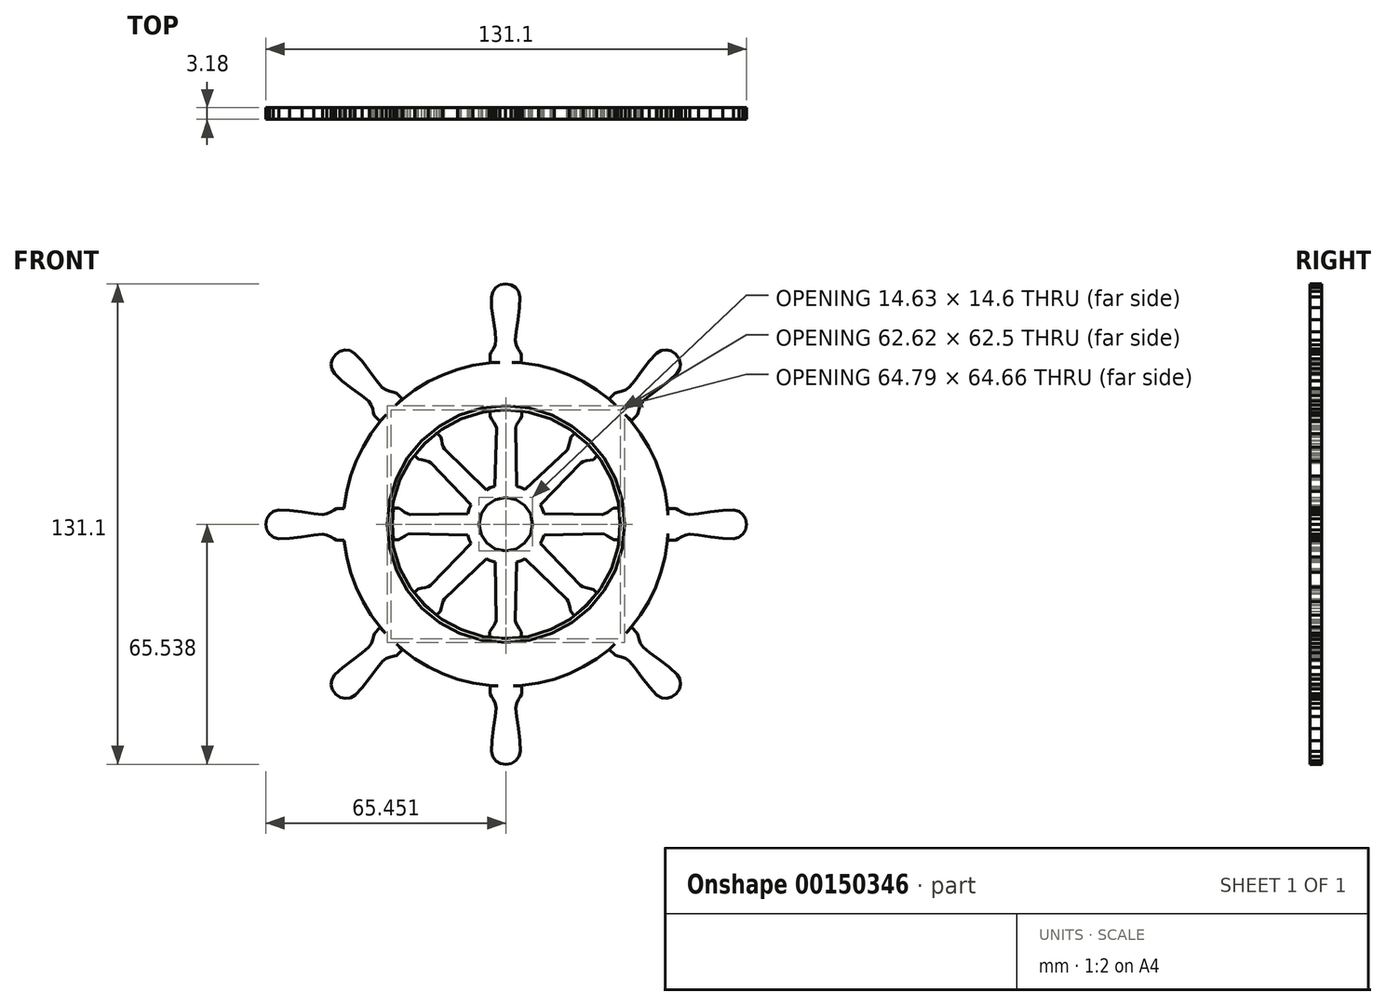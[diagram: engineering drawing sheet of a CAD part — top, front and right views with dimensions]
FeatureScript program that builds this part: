
annotation { "Feature Type Name" : "Feature", "Feature Type Description" : "" }
export const myFeature = defineFeature(function(context is Context, id is Id, definition is map)
    precondition{}
    {
        {
            var Q0;
            Q0=qCreatedBy(makeId("Front.planeOp"),FACE);
            var sketch = newSketch(context, id + "F0", { "sketchPlane" : qUnion([Q0])});
            skLineSegment(sketch, "E0", {"start": v(-9.65, -2.99) * mm, "end": v(-26.1, -2.56) * mm});
            skLineSegment(sketch, "E1", {"start": v(-26.1, -2.56) * mm, "end": v(-26.82, -2.77) * mm});
            skLineSegment(sketch, "E2", {"start": v(-26.82, -2.77) * mm, "end": v(-27.64, -3.22) * mm});
            skLineSegment(sketch, "E3", {"start": v(-27.64, -3.22) * mm, "end": v(-28.5, -3.78) * mm});
            skLineSegment(sketch, "E4", {"start": v(-28.5, -3.78) * mm, "end": v(-29.36, -4.29) * mm});
            skLineSegment(sketch, "E5", {"start": v(-29.36, -4.29) * mm, "end": v(-30.78, -4.29) * mm});
            skLineSegment(sketch, "E6", {"start": v(-30.78, -4.29) * mm, "end": v(-31.08, 0.04) * mm});
            skLineSegment(sketch, "E7", {"start": v(-31.08, 0.04) * mm, "end": v(-30.78, 4.37) * mm});
            skLineSegment(sketch, "E8", {"start": v(-30.78, 4.37) * mm, "end": v(-29.29, 4.37) * mm});
            skLineSegment(sketch, "E9", {"start": v(-29.29, 4.37) * mm, "end": v(-28.5, 3.85) * mm});
            skLineSegment(sketch, "E10", {"start": v(-28.5, 3.85) * mm, "end": v(-27.69, 3.29) * mm});
            skLineSegment(sketch, "E11", {"start": v(-27.69, 3.29) * mm, "end": v(-26.91, 2.84) * mm});
            skLineSegment(sketch, "E12", {"start": v(-26.91, 2.84) * mm, "end": v(-26.22, 2.67) * mm});
            skLineSegment(sketch, "E13", {"start": v(-26.22, 2.67) * mm, "end": v(-9.66, 2.93) * mm});
            skLineSegment(sketch, "E14", {"start": v(-29.33, -4.38) * mm, "end": v(-29.55, 0) * mm});
            skLineSegment(sketch, "E15", {"start": v(-29.55, 0) * mm, "end": v(-29.33, 4.44) * mm});
            skLineSegment(sketch, "E16", {"start": v(-62.02, -3.96) * mm, "end": v(-59.16, -3.9) * mm});
            skLineSegment(sketch, "E17", {"start": v(-59.16, -3.9) * mm, "end": v(-55.76, -3.45) * mm});
            skLineSegment(sketch, "E18", {"start": v(-55.76, -3.45) * mm, "end": v(-52.53, -2.95) * mm});
            skLineSegment(sketch, "E19", {"start": v(-52.53, -2.95) * mm, "end": v(-50.15, -2.7) * mm});
            skLineSegment(sketch, "E20", {"start": v(-50.15, -2.7) * mm, "end": v(-48.91, -2.92) * mm});
            skLineSegment(sketch, "E21", {"start": v(-48.91, -2.92) * mm, "end": v(-47.83, -3.44) * mm});
            skLineSegment(sketch, "E22", {"start": v(-47.83, -3.44) * mm, "end": v(-46.94, -3.98) * mm});
            skLineSegment(sketch, "E23", {"start": v(-46.94, -3.98) * mm, "end": v(-46.3, -4.31) * mm});
            skLineSegment(sketch, "E24", {"start": v(-46.3, -4.31) * mm, "end": v(-44.13, -4.33) * mm});
            skLineSegment(sketch, "E25", {"start": v(-44.13, -4.33) * mm, "end": v(-44.13, 4.25) * mm});
            skLineSegment(sketch, "E26", {"start": v(-44.13, 4.25) * mm, "end": v(-46.3, 4.23) * mm});
            skLineSegment(sketch, "E27", {"start": v(-46.3, 4.23) * mm, "end": v(-46.94, 3.9) * mm});
            skLineSegment(sketch, "E28", {"start": v(-46.94, 3.9) * mm, "end": v(-47.83, 3.36) * mm});
            skLineSegment(sketch, "E29", {"start": v(-47.83, 3.36) * mm, "end": v(-48.91, 2.85) * mm});
            skLineSegment(sketch, "E30", {"start": v(-48.91, 2.85) * mm, "end": v(-50.15, 2.62) * mm});
            skLineSegment(sketch, "E31", {"start": v(-50.15, 2.62) * mm, "end": v(-52.53, 2.85) * mm});
            skLineSegment(sketch, "E32", {"start": v(-52.53, 2.85) * mm, "end": v(-55.75, 3.32) * mm});
            skLineSegment(sketch, "E33", {"start": v(-55.75, 3.32) * mm, "end": v(-59.15, 3.75) * mm});
            skLineSegment(sketch, "E34", {"start": v(-59.15, 3.75) * mm, "end": v(-62.02, 3.87) * mm});
            skLineSegment(sketch, "E35", {"start": v(-62.02, 3.87) * mm, "end": v(-63.52, 3.5) * mm});
            skLineSegment(sketch, "E36", {"start": v(-63.52, 3.5) * mm, "end": v(-64.63, 2.66) * mm});
            skLineSegment(sketch, "E37", {"start": v(-64.63, 2.66) * mm, "end": v(-65.32, 1.44) * mm});
            skLineSegment(sketch, "E38", {"start": v(-65.32, 1.44) * mm, "end": v(-65.55, -0.04) * mm});
            skLineSegment(sketch, "E39", {"start": v(-65.55, -0.04) * mm, "end": v(-65.3, -1.56) * mm});
            skLineSegment(sketch, "E40", {"start": v(-65.3, -1.56) * mm, "end": v(-64.57, -2.76) * mm});
            skLineSegment(sketch, "E41", {"start": v(-64.57, -2.76) * mm, "end": v(-63.45, -3.57) * mm});
            skLineSegment(sketch, "E42", {"start": v(-63.45, -3.57) * mm, "end": v(-62.02, -3.96) * mm});
            skLineSegment(sketch, "E43", {"start": v(-46.16, -4.38) * mm, "end": v(-46.53, -0.02) * mm});
            skLineSegment(sketch, "E44", {"start": v(-46.53, -0.02) * mm, "end": v(-46.16, 4.33) * mm});
            skLineSegment(sketch, "E45", {"start": v(2.89, -9.76) * mm, "end": v(2.46, -26.18) * mm});
            skLineSegment(sketch, "E46", {"start": v(2.46, -26.18) * mm, "end": v(2.67, -26.9) * mm});
            skLineSegment(sketch, "E47", {"start": v(2.67, -26.9) * mm, "end": v(3.12, -27.72) * mm});
            skLineSegment(sketch, "E48", {"start": v(3.12, -27.72) * mm, "end": v(3.68, -28.58) * mm});
            skLineSegment(sketch, "E49", {"start": v(3.68, -28.58) * mm, "end": v(4.19, -29.44) * mm});
            skLineSegment(sketch, "E50", {"start": v(4.19, -29.44) * mm, "end": v(4.19, -30.85) * mm});
            skLineSegment(sketch, "E51", {"start": v(4.19, -30.85) * mm, "end": v(-0.15, -31.15) * mm});
            skLineSegment(sketch, "E52", {"start": v(-0.15, -31.15) * mm, "end": v(-4.49, -30.85) * mm});
            skLineSegment(sketch, "E53", {"start": v(-4.49, -30.85) * mm, "end": v(-4.49, -29.36) * mm});
            skLineSegment(sketch, "E54", {"start": v(-4.49, -29.36) * mm, "end": v(-3.97, -28.57) * mm});
            skLineSegment(sketch, "E55", {"start": v(-3.97, -28.57) * mm, "end": v(-3.4, -27.76) * mm});
            skLineSegment(sketch, "E56", {"start": v(-3.4, -27.76) * mm, "end": v(-2.96, -27) * mm});
            skLineSegment(sketch, "E57", {"start": v(-2.96, -27) * mm, "end": v(-2.79, -26.3) * mm});
            skLineSegment(sketch, "E58", {"start": v(-2.79, -26.3) * mm, "end": v(-3.05, -9.77) * mm});
            skLineSegment(sketch, "E59", {"start": v(4.28, -29.4) * mm, "end": v(-0.1, -29.62) * mm});
            skLineSegment(sketch, "E60", {"start": v(-0.1, -29.62) * mm, "end": v(-4.56, -29.4) * mm});
            skLineSegment(sketch, "E61", {"start": v(3.86, -62.02) * mm, "end": v(3.79, -59.17) * mm});
            skLineSegment(sketch, "E62", {"start": v(3.79, -59.17) * mm, "end": v(3.34, -55.78) * mm});
            skLineSegment(sketch, "E63", {"start": v(3.34, -55.78) * mm, "end": v(2.84, -52.55) * mm});
            skLineSegment(sketch, "E64", {"start": v(2.84, -52.55) * mm, "end": v(2.6, -50.18) * mm});
            skLineSegment(sketch, "E65", {"start": v(2.6, -50.18) * mm, "end": v(2.82, -48.95) * mm});
            skLineSegment(sketch, "E66", {"start": v(2.82, -48.95) * mm, "end": v(3.33, -47.86) * mm});
            skLineSegment(sketch, "E67", {"start": v(3.33, -47.86) * mm, "end": v(3.88, -46.98) * mm});
            skLineSegment(sketch, "E68", {"start": v(3.88, -46.98) * mm, "end": v(4.21, -46.34) * mm});
            skLineSegment(sketch, "E69", {"start": v(4.21, -46.34) * mm, "end": v(4.23, -44.17) * mm});
            skLineSegment(sketch, "E70", {"start": v(4.23, -44.17) * mm, "end": v(-4.37, -44.17) * mm});
            skLineSegment(sketch, "E71", {"start": v(-4.37, -44.17) * mm, "end": v(-4.35, -46.34) * mm});
            skLineSegment(sketch, "E72", {"start": v(-4.35, -46.34) * mm, "end": v(-4.02, -46.98) * mm});
            skLineSegment(sketch, "E73", {"start": v(-4.02, -46.98) * mm, "end": v(-3.48, -47.86) * mm});
            skLineSegment(sketch, "E74", {"start": v(-3.48, -47.86) * mm, "end": v(-2.96, -48.95) * mm});
            skLineSegment(sketch, "E75", {"start": v(-2.96, -48.95) * mm, "end": v(-2.74, -50.18) * mm});
            skLineSegment(sketch, "E76", {"start": v(-2.74, -50.18) * mm, "end": v(-2.97, -52.55) * mm});
            skLineSegment(sketch, "E77", {"start": v(-2.97, -52.55) * mm, "end": v(-3.44, -55.77) * mm});
            skLineSegment(sketch, "E78", {"start": v(-3.44, -55.77) * mm, "end": v(-3.87, -59.16) * mm});
            skLineSegment(sketch, "E79", {"start": v(-3.87, -59.16) * mm, "end": v(-3.99, -62.02) * mm});
            skLineSegment(sketch, "E80", {"start": v(-3.99, -62.02) * mm, "end": v(-3.62, -63.52) * mm});
            skLineSegment(sketch, "E81", {"start": v(-3.62, -63.52) * mm, "end": v(-2.77, -64.63) * mm});
            skLineSegment(sketch, "E82", {"start": v(-2.77, -64.63) * mm, "end": v(-1.55, -65.31) * mm});
            skLineSegment(sketch, "E83", {"start": v(-1.55, -65.31) * mm, "end": v(-0.07, -65.55) * mm});
            skLineSegment(sketch, "E84", {"start": v(-0.07, -65.55) * mm, "end": v(1.46, -65.3) * mm});
            skLineSegment(sketch, "E85", {"start": v(1.46, -65.3) * mm, "end": v(2.65, -64.57) * mm});
            skLineSegment(sketch, "E86", {"start": v(2.65, -64.57) * mm, "end": v(3.47, -63.46) * mm});
            skLineSegment(sketch, "E87", {"start": v(3.47, -63.46) * mm, "end": v(3.86, -62.02) * mm});
            skLineSegment(sketch, "E88", {"start": v(4.27, -46.2) * mm, "end": v(-0.09, -46.56) * mm});
            skLineSegment(sketch, "E89", {"start": v(-0.09, -46.56) * mm, "end": v(-4.45, -46.2) * mm});
            skLineSegment(sketch, "E90", {"start": v(-3.08, 9.76) * mm, "end": v(-2.66, 26.18) * mm});
            skLineSegment(sketch, "E91", {"start": v(-2.66, 26.18) * mm, "end": v(-2.86, 26.9) * mm});
            skLineSegment(sketch, "E92", {"start": v(-2.86, 26.9) * mm, "end": v(-3.32, 27.72) * mm});
            skLineSegment(sketch, "E93", {"start": v(-3.32, 27.72) * mm, "end": v(-3.88, 28.58) * mm});
            skLineSegment(sketch, "E94", {"start": v(-3.88, 28.58) * mm, "end": v(-4.38, 29.44) * mm});
            skLineSegment(sketch, "E95", {"start": v(-4.38, 29.44) * mm, "end": v(-4.38, 30.85) * mm});
            skLineSegment(sketch, "E96", {"start": v(-4.38, 30.85) * mm, "end": v(-0.05, 31.15) * mm});
            skLineSegment(sketch, "E97", {"start": v(-0.05, 31.15) * mm, "end": v(4.29, 30.85) * mm});
            skLineSegment(sketch, "E98", {"start": v(4.29, 30.85) * mm, "end": v(4.29, 29.36) * mm});
            skLineSegment(sketch, "E99", {"start": v(4.29, 29.36) * mm, "end": v(3.77, 28.57) * mm});
            skLineSegment(sketch, "E100", {"start": v(3.77, 28.57) * mm, "end": v(3.2, 27.76) * mm});
            skLineSegment(sketch, "E101", {"start": v(3.2, 27.76) * mm, "end": v(2.76, 27) * mm});
            skLineSegment(sketch, "E102", {"start": v(2.76, 27) * mm, "end": v(2.59, 26.3) * mm});
            skLineSegment(sketch, "E103", {"start": v(2.59, 26.3) * mm, "end": v(2.85, 9.77) * mm});
            skLineSegment(sketch, "E104", {"start": v(-4.48, 29.4) * mm, "end": v(-0.1, 29.62) * mm});
            skLineSegment(sketch, "E105", {"start": v(-0.1, 29.62) * mm, "end": v(4.36, 29.4) * mm});
            skLineSegment(sketch, "E106", {"start": v(-4.05, 62.02) * mm, "end": v(-3.99, 59.17) * mm});
            skLineSegment(sketch, "E107", {"start": v(-3.99, 59.17) * mm, "end": v(-3.54, 55.78) * mm});
            skLineSegment(sketch, "E108", {"start": v(-3.54, 55.78) * mm, "end": v(-3.04, 52.56) * mm});
            skLineSegment(sketch, "E109", {"start": v(-3.04, 52.56) * mm, "end": v(-2.8, 50.18) * mm});
            skLineSegment(sketch, "E110", {"start": v(-2.8, 50.18) * mm, "end": v(-3.02, 48.95) * mm});
            skLineSegment(sketch, "E111", {"start": v(-3.02, 48.95) * mm, "end": v(-3.53, 47.86) * mm});
            skLineSegment(sketch, "E112", {"start": v(-3.53, 47.86) * mm, "end": v(-4.08, 46.98) * mm});
            skLineSegment(sketch, "E113", {"start": v(-4.08, 46.98) * mm, "end": v(-4.4, 46.34) * mm});
            skLineSegment(sketch, "E114", {"start": v(-4.4, 46.34) * mm, "end": v(-4.43, 44.17) * mm});
            skLineSegment(sketch, "E115", {"start": v(-4.43, 44.17) * mm, "end": v(4.17, 44.17) * mm});
            skLineSegment(sketch, "E116", {"start": v(4.17, 44.17) * mm, "end": v(4.15, 46.34) * mm});
            skLineSegment(sketch, "E117", {"start": v(4.15, 46.34) * mm, "end": v(3.82, 46.98) * mm});
            skLineSegment(sketch, "E118", {"start": v(3.82, 46.98) * mm, "end": v(3.28, 47.86) * mm});
            skLineSegment(sketch, "E119", {"start": v(3.28, 47.86) * mm, "end": v(2.76, 48.95) * mm});
            skLineSegment(sketch, "E120", {"start": v(2.76, 48.95) * mm, "end": v(2.54, 50.18) * mm});
            skLineSegment(sketch, "E121", {"start": v(2.54, 50.18) * mm, "end": v(2.77, 52.55) * mm});
            skLineSegment(sketch, "E122", {"start": v(2.77, 52.55) * mm, "end": v(3.24, 55.77) * mm});
            skLineSegment(sketch, "E123", {"start": v(3.24, 55.77) * mm, "end": v(3.67, 59.16) * mm});
            skLineSegment(sketch, "E124", {"start": v(3.67, 59.16) * mm, "end": v(3.8, 62.02) * mm});
            skLineSegment(sketch, "E125", {"start": v(3.8, 62.02) * mm, "end": v(3.42, 63.52) * mm});
            skLineSegment(sketch, "E126", {"start": v(3.42, 63.52) * mm, "end": v(2.57, 64.63) * mm});
            skLineSegment(sketch, "E127", {"start": v(2.57, 64.63) * mm, "end": v(1.35, 65.32) * mm});
            skLineSegment(sketch, "E128", {"start": v(1.35, 65.32) * mm, "end": v(-0.13, 65.55) * mm});
            skLineSegment(sketch, "E129", {"start": v(-0.13, 65.55) * mm, "end": v(-1.65, 65.3) * mm});
            skLineSegment(sketch, "E130", {"start": v(-1.65, 65.3) * mm, "end": v(-2.85, 64.57) * mm});
            skLineSegment(sketch, "E131", {"start": v(-2.85, 64.57) * mm, "end": v(-3.67, 63.46) * mm});
            skLineSegment(sketch, "E132", {"start": v(-3.67, 63.46) * mm, "end": v(-4.05, 62.02) * mm});
            skLineSegment(sketch, "E133", {"start": v(-4.47, 46.2) * mm, "end": v(-0.11, 46.57) * mm});
            skLineSegment(sketch, "E134", {"start": v(-0.11, 46.57) * mm, "end": v(4.25, 46.2) * mm});
            skLineSegment(sketch, "E135", {"start": v(8.93, -4.8) * mm, "end": v(20.26, -16.7) * mm});
            skLineSegment(sketch, "E136", {"start": v(20.26, -16.7) * mm, "end": v(20.92, -17.07) * mm});
            skLineSegment(sketch, "E137", {"start": v(20.92, -17.07) * mm, "end": v(21.82, -17.33) * mm});
            skLineSegment(sketch, "E138", {"start": v(21.82, -17.33) * mm, "end": v(22.82, -17.54) * mm});
            skLineSegment(sketch, "E139", {"start": v(22.82, -17.54) * mm, "end": v(23.79, -17.8) * mm});
            skLineSegment(sketch, "E140", {"start": v(23.79, -17.8) * mm, "end": v(24.79, -18.79) * mm});
            skLineSegment(sketch, "E141", {"start": v(24.79, -18.79) * mm, "end": v(21.94, -22.07) * mm});
            skLineSegment(sketch, "E142", {"start": v(21.94, -22.07) * mm, "end": v(18.65, -24.9) * mm});
            skLineSegment(sketch, "E143", {"start": v(18.65, -24.9) * mm, "end": v(17.6, -23.86) * mm});
            skLineSegment(sketch, "E144", {"start": v(17.6, -23.86) * mm, "end": v(17.4, -22.93) * mm});
            skLineSegment(sketch, "E145", {"start": v(17.4, -22.93) * mm, "end": v(17.24, -21.96) * mm});
            skLineSegment(sketch, "E146", {"start": v(17.24, -21.96) * mm, "end": v(17, -21.1) * mm});
            skLineSegment(sketch, "E147", {"start": v(17, -21.1) * mm, "end": v(16.63, -20.5) * mm});
            skLineSegment(sketch, "E148", {"start": v(16.63, -20.5) * mm, "end": v(4.74, -9) * mm});
            skLineSegment(sketch, "E149", {"start": v(23.83, -17.7) * mm, "end": v(20.88, -20.95) * mm});
            skLineSegment(sketch, "E150", {"start": v(20.88, -20.95) * mm, "end": v(17.58, -23.94) * mm});
            skLineSegment(sketch, "E151", {"start": v(46.64, -41.07) * mm, "end": v(44.57, -39.1) * mm});
            skLineSegment(sketch, "E152", {"start": v(44.57, -39.1) * mm, "end": v(41.86, -37.01) * mm});
            skLineSegment(sketch, "E153", {"start": v(41.86, -37.01) * mm, "end": v(39.22, -35.08) * mm});
            skLineSegment(sketch, "E154", {"start": v(39.22, -35.08) * mm, "end": v(37.36, -33.58) * mm});
            skLineSegment(sketch, "E155", {"start": v(37.36, -33.58) * mm, "end": v(36.65, -32.55) * mm});
            skLineSegment(sketch, "E156", {"start": v(36.65, -32.55) * mm, "end": v(36.24, -31.42) * mm});
            skLineSegment(sketch, "E157", {"start": v(36.24, -31.42) * mm, "end": v(36, -30.4) * mm});
            skLineSegment(sketch, "E158", {"start": v(36, -30.4) * mm, "end": v(35.78, -29.73) * mm});
            skLineSegment(sketch, "E159", {"start": v(35.78, -29.73) * mm, "end": v(34.26, -28.18) * mm});
            skLineSegment(sketch, "E160", {"start": v(34.26, -28.18) * mm, "end": v(28.18, -34.25) * mm});
            skLineSegment(sketch, "E161", {"start": v(28.18, -34.25) * mm, "end": v(29.73, -35.77) * mm});
            skLineSegment(sketch, "E162", {"start": v(29.73, -35.77) * mm, "end": v(30.41, -35.99) * mm});
            skLineSegment(sketch, "E163", {"start": v(30.41, -35.99) * mm, "end": v(31.43, -36.23) * mm});
            skLineSegment(sketch, "E164", {"start": v(31.43, -36.23) * mm, "end": v(32.56, -36.63) * mm});
            skLineSegment(sketch, "E165", {"start": v(32.56, -36.63) * mm, "end": v(33.59, -37.35) * mm});
            skLineSegment(sketch, "E166", {"start": v(33.59, -37.35) * mm, "end": v(35.1, -39.18) * mm});
            skLineSegment(sketch, "E167", {"start": v(35.1, -39.18) * mm, "end": v(37.06, -41.8) * mm});
            skLineSegment(sketch, "E168", {"start": v(37.06, -41.8) * mm, "end": v(39.15, -44.5) * mm});
            skLineSegment(sketch, "E169", {"start": v(39.15, -44.5) * mm, "end": v(41.1, -46.6) * mm});
            skLineSegment(sketch, "E170", {"start": v(41.1, -46.6) * mm, "end": v(42.42, -47.4) * mm});
            skLineSegment(sketch, "E171", {"start": v(42.42, -47.4) * mm, "end": v(43.8, -47.58) * mm});
            skLineSegment(sketch, "E172", {"start": v(43.8, -47.58) * mm, "end": v(45.15, -47.2) * mm});
            skLineSegment(sketch, "E173", {"start": v(45.15, -47.2) * mm, "end": v(46.37, -46.33) * mm});
            skLineSegment(sketch, "E174", {"start": v(46.37, -46.33) * mm, "end": v(47.26, -45.07) * mm});
            skLineSegment(sketch, "E175", {"start": v(47.26, -45.07) * mm, "end": v(47.6, -43.72) * mm});
            skLineSegment(sketch, "E176", {"start": v(47.6, -43.72) * mm, "end": v(47.39, -42.35) * mm});
            skLineSegment(sketch, "E177", {"start": v(47.39, -42.35) * mm, "end": v(46.64, -41.07) * mm});
            skLineSegment(sketch, "E178", {"start": v(35.73, -29.58) * mm, "end": v(32.9, -32.92) * mm});
            skLineSegment(sketch, "E179", {"start": v(32.9, -32.92) * mm, "end": v(29.56, -35.74) * mm});
            skLineSegment(sketch, "E180", {"start": v(-9.13, 4.8) * mm, "end": v(-20.46, 16.7) * mm});
            skLineSegment(sketch, "E181", {"start": v(-20.46, 16.7) * mm, "end": v(-21.12, 17.07) * mm});
            skLineSegment(sketch, "E182", {"start": v(-21.12, 17.07) * mm, "end": v(-22.02, 17.33) * mm});
            skLineSegment(sketch, "E183", {"start": v(-22.02, 17.33) * mm, "end": v(-23.02, 17.55) * mm});
            skLineSegment(sketch, "E184", {"start": v(-23.02, 17.55) * mm, "end": v(-23.98, 17.8) * mm});
            skLineSegment(sketch, "E185", {"start": v(-23.98, 17.8) * mm, "end": v(-24.98, 18.79) * mm});
            skLineSegment(sketch, "E186", {"start": v(-24.98, 18.79) * mm, "end": v(-22.14, 22.07) * mm});
            skLineSegment(sketch, "E187", {"start": v(-22.14, 22.07) * mm, "end": v(-18.85, 24.9) * mm});
            skLineSegment(sketch, "E188", {"start": v(-18.85, 24.9) * mm, "end": v(-17.8, 23.86) * mm});
            skLineSegment(sketch, "E189", {"start": v(-17.8, 23.86) * mm, "end": v(-17.6, 22.93) * mm});
            skLineSegment(sketch, "E190", {"start": v(-17.6, 22.93) * mm, "end": v(-17.43, 21.97) * mm});
            skLineSegment(sketch, "E191", {"start": v(-17.43, 21.97) * mm, "end": v(-17.2, 21.1) * mm});
            skLineSegment(sketch, "E192", {"start": v(-17.2, 21.1) * mm, "end": v(-16.83, 20.5) * mm});
            skLineSegment(sketch, "E193", {"start": v(-16.83, 20.5) * mm, "end": v(-4.94, 9) * mm});
            skLineSegment(sketch, "E194", {"start": v(-24.03, 17.7) * mm, "end": v(-21.08, 20.95) * mm});
            skLineSegment(sketch, "E195", {"start": v(-21.08, 20.95) * mm, "end": v(-17.78, 23.94) * mm});
            skLineSegment(sketch, "E196", {"start": v(-46.84, 41.07) * mm, "end": v(-44.77, 39.1) * mm});
            skLineSegment(sketch, "E197", {"start": v(-44.77, 39.1) * mm, "end": v(-42.06, 37.01) * mm});
            skLineSegment(sketch, "E198", {"start": v(-42.06, 37.01) * mm, "end": v(-39.42, 35.09) * mm});
            skLineSegment(sketch, "E199", {"start": v(-39.42, 35.09) * mm, "end": v(-37.56, 33.58) * mm});
            skLineSegment(sketch, "E200", {"start": v(-37.56, 33.58) * mm, "end": v(-36.84, 32.55) * mm});
            skLineSegment(sketch, "E201", {"start": v(-36.84, 32.55) * mm, "end": v(-36.44, 31.42) * mm});
            skLineSegment(sketch, "E202", {"start": v(-36.44, 31.42) * mm, "end": v(-36.2, 30.4) * mm});
            skLineSegment(sketch, "E203", {"start": v(-36.2, 30.4) * mm, "end": v(-35.98, 29.73) * mm});
            skLineSegment(sketch, "E204", {"start": v(-35.98, 29.73) * mm, "end": v(-34.45, 28.18) * mm});
            skLineSegment(sketch, "E205", {"start": v(-34.45, 28.18) * mm, "end": v(-28.38, 34.25) * mm});
            skLineSegment(sketch, "E206", {"start": v(-28.38, 34.25) * mm, "end": v(-29.93, 35.77) * mm});
            skLineSegment(sketch, "E207", {"start": v(-29.93, 35.77) * mm, "end": v(-30.61, 35.99) * mm});
            skLineSegment(sketch, "E208", {"start": v(-30.61, 35.99) * mm, "end": v(-31.62, 36.23) * mm});
            skLineSegment(sketch, "E209", {"start": v(-31.62, 36.23) * mm, "end": v(-32.76, 36.63) * mm});
            skLineSegment(sketch, "E210", {"start": v(-32.76, 36.63) * mm, "end": v(-33.79, 37.35) * mm});
            skLineSegment(sketch, "E211", {"start": v(-33.79, 37.35) * mm, "end": v(-35.3, 39.18) * mm});
            skLineSegment(sketch, "E212", {"start": v(-35.3, 39.18) * mm, "end": v(-37.26, 41.8) * mm});
            skLineSegment(sketch, "E213", {"start": v(-37.26, 41.8) * mm, "end": v(-39.35, 44.5) * mm});
            skLineSegment(sketch, "E214", {"start": v(-39.35, 44.5) * mm, "end": v(-41.3, 46.6) * mm});
            skLineSegment(sketch, "E215", {"start": v(-41.3, 46.6) * mm, "end": v(-42.62, 47.4) * mm});
            skLineSegment(sketch, "E216", {"start": v(-42.62, 47.4) * mm, "end": v(-44, 47.59) * mm});
            skLineSegment(sketch, "E217", {"start": v(-44, 47.59) * mm, "end": v(-45.35, 47.21) * mm});
            skLineSegment(sketch, "E218", {"start": v(-45.35, 47.21) * mm, "end": v(-46.57, 46.33) * mm});
            skLineSegment(sketch, "E219", {"start": v(-46.57, 46.33) * mm, "end": v(-47.46, 45.07) * mm});
            skLineSegment(sketch, "E220", {"start": v(-47.46, 45.07) * mm, "end": v(-47.8, 43.72) * mm});
            skLineSegment(sketch, "E221", {"start": v(-47.8, 43.72) * mm, "end": v(-47.58, 42.35) * mm});
            skLineSegment(sketch, "E222", {"start": v(-47.58, 42.35) * mm, "end": v(-46.84, 41.07) * mm});
            skLineSegment(sketch, "E223", {"start": v(-35.92, 29.58) * mm, "end": v(-33.1, 32.92) * mm});
            skLineSegment(sketch, "E224", {"start": v(-33.1, 32.92) * mm, "end": v(-29.76, 35.74) * mm});
            skLineSegment(sketch, "E225", {"start": v(-4.9, -9) * mm, "end": v(-16.84, -20.32) * mm});
            skLineSegment(sketch, "E226", {"start": v(-16.84, -20.32) * mm, "end": v(-17.2, -20.97) * mm});
            skLineSegment(sketch, "E227", {"start": v(-17.2, -20.97) * mm, "end": v(-17.46, -21.87) * mm});
            skLineSegment(sketch, "E228", {"start": v(-17.46, -21.87) * mm, "end": v(-17.68, -22.88) * mm});
            skLineSegment(sketch, "E229", {"start": v(-17.68, -22.88) * mm, "end": v(-17.93, -23.84) * mm});
            skLineSegment(sketch, "E230", {"start": v(-17.93, -23.84) * mm, "end": v(-18.93, -24.83) * mm});
            skLineSegment(sketch, "E231", {"start": v(-18.93, -24.83) * mm, "end": v(-22.2, -22) * mm});
            skLineSegment(sketch, "E232", {"start": v(-22.2, -22) * mm, "end": v(-25.06, -18.72) * mm});
            skLineSegment(sketch, "E233", {"start": v(-25.06, -18.72) * mm, "end": v(-24, -17.66) * mm});
            skLineSegment(sketch, "E234", {"start": v(-24, -17.66) * mm, "end": v(-23.08, -17.47) * mm});
            skLineSegment(sketch, "E235", {"start": v(-23.08, -17.47) * mm, "end": v(-22.1, -17.3) * mm});
            skLineSegment(sketch, "E236", {"start": v(-22.1, -17.3) * mm, "end": v(-21.24, -17.07) * mm});
            skLineSegment(sketch, "E237", {"start": v(-21.24, -17.07) * mm, "end": v(-20.63, -16.7) * mm});
            skLineSegment(sketch, "E238", {"start": v(-20.63, -16.7) * mm, "end": v(-9.1, -4.83) * mm});
            skLineSegment(sketch, "E239", {"start": v(-17.84, -23.88) * mm, "end": v(-21.09, -20.94) * mm});
            skLineSegment(sketch, "E240", {"start": v(-21.09, -20.94) * mm, "end": v(-24.09, -17.65) * mm});
            skLineSegment(sketch, "E241", {"start": v(-41.25, -46.65) * mm, "end": v(-39.27, -44.58) * mm});
            skLineSegment(sketch, "E242", {"start": v(-39.27, -44.58) * mm, "end": v(-37.19, -41.87) * mm});
            skLineSegment(sketch, "E243", {"start": v(-37.19, -41.87) * mm, "end": v(-35.26, -39.24) * mm});
            skLineSegment(sketch, "E244", {"start": v(-35.26, -39.24) * mm, "end": v(-33.75, -37.39) * mm});
            skLineSegment(sketch, "E245", {"start": v(-33.75, -37.39) * mm, "end": v(-32.72, -36.67) * mm});
            skLineSegment(sketch, "E246", {"start": v(-32.72, -36.67) * mm, "end": v(-31.58, -36.27) * mm});
            skLineSegment(sketch, "E247", {"start": v(-31.58, -36.27) * mm, "end": v(-30.57, -36.03) * mm});
            skLineSegment(sketch, "E248", {"start": v(-30.57, -36.03) * mm, "end": v(-29.89, -35.81) * mm});
            skLineSegment(sketch, "E249", {"start": v(-29.89, -35.81) * mm, "end": v(-28.34, -34.29) * mm});
            skLineSegment(sketch, "E250", {"start": v(-28.34, -34.29) * mm, "end": v(-34.41, -28.22) * mm});
            skLineSegment(sketch, "E251", {"start": v(-34.41, -28.22) * mm, "end": v(-35.94, -29.77) * mm});
            skLineSegment(sketch, "E252", {"start": v(-35.94, -29.77) * mm, "end": v(-36.16, -30.45) * mm});
            skLineSegment(sketch, "E253", {"start": v(-36.16, -30.45) * mm, "end": v(-36.4, -31.46) * mm});
            skLineSegment(sketch, "E254", {"start": v(-36.4, -31.46) * mm, "end": v(-36.8, -32.6) * mm});
            skLineSegment(sketch, "E255", {"start": v(-36.8, -32.6) * mm, "end": v(-37.52, -33.62) * mm});
            skLineSegment(sketch, "E256", {"start": v(-37.52, -33.62) * mm, "end": v(-39.36, -35.14) * mm});
            skLineSegment(sketch, "E257", {"start": v(-39.36, -35.14) * mm, "end": v(-41.97, -37.08) * mm});
            skLineSegment(sketch, "E258", {"start": v(-41.97, -37.08) * mm, "end": v(-44.68, -39.17) * mm});
            skLineSegment(sketch, "E259", {"start": v(-44.68, -39.17) * mm, "end": v(-46.8, -41.11) * mm});
            skLineSegment(sketch, "E260", {"start": v(-46.8, -41.11) * mm, "end": v(-47.6, -42.43) * mm});
            skLineSegment(sketch, "E261", {"start": v(-47.6, -42.43) * mm, "end": v(-47.78, -43.81) * mm});
            skLineSegment(sketch, "E262", {"start": v(-47.78, -43.81) * mm, "end": v(-47.4, -45.16) * mm});
            skLineSegment(sketch, "E263", {"start": v(-47.4, -45.16) * mm, "end": v(-46.52, -46.37) * mm});
            skLineSegment(sketch, "E264", {"start": v(-46.52, -46.37) * mm, "end": v(-45.26, -47.27) * mm});
            skLineSegment(sketch, "E265", {"start": v(-45.26, -47.27) * mm, "end": v(-43.9, -47.6) * mm});
            skLineSegment(sketch, "E266", {"start": v(-43.9, -47.6) * mm, "end": v(-42.54, -47.39) * mm});
            skLineSegment(sketch, "E267", {"start": v(-42.54, -47.39) * mm, "end": v(-41.25, -46.65) * mm});
            skLineSegment(sketch, "E268", {"start": v(-29.74, -35.75) * mm, "end": v(-33.08, -32.93) * mm});
            skLineSegment(sketch, "E269", {"start": v(-33.08, -32.93) * mm, "end": v(-35.9, -29.6) * mm});
            skLineSegment(sketch, "E270", {"start": v(4.7, 9) * mm, "end": v(16.64, 20.32) * mm});
            skLineSegment(sketch, "E271", {"start": v(16.64, 20.32) * mm, "end": v(17, 20.97) * mm});
            skLineSegment(sketch, "E272", {"start": v(17, 20.97) * mm, "end": v(17.26, 21.88) * mm});
            skLineSegment(sketch, "E273", {"start": v(17.26, 21.88) * mm, "end": v(17.48, 22.88) * mm});
            skLineSegment(sketch, "E274", {"start": v(17.48, 22.88) * mm, "end": v(17.73, 23.84) * mm});
            skLineSegment(sketch, "E275", {"start": v(17.73, 23.84) * mm, "end": v(18.73, 24.84) * mm});
            skLineSegment(sketch, "E276", {"start": v(18.73, 24.84) * mm, "end": v(22.01, 22) * mm});
            skLineSegment(sketch, "E277", {"start": v(22.01, 22) * mm, "end": v(24.86, 18.72) * mm});
            skLineSegment(sketch, "E278", {"start": v(24.86, 18.72) * mm, "end": v(23.8, 17.66) * mm});
            skLineSegment(sketch, "E279", {"start": v(23.8, 17.66) * mm, "end": v(22.88, 17.47) * mm});
            skLineSegment(sketch, "E280", {"start": v(22.88, 17.47) * mm, "end": v(21.9, 17.3) * mm});
            skLineSegment(sketch, "E281", {"start": v(21.9, 17.3) * mm, "end": v(21.04, 17.07) * mm});
            skLineSegment(sketch, "E282", {"start": v(21.04, 17.07) * mm, "end": v(20.43, 16.7) * mm});
            skLineSegment(sketch, "E283", {"start": v(20.43, 16.7) * mm, "end": v(8.91, 4.83) * mm});
            skLineSegment(sketch, "E284", {"start": v(17.64, 23.88) * mm, "end": v(20.89, 20.94) * mm});
            skLineSegment(sketch, "E285", {"start": v(20.89, 20.94) * mm, "end": v(23.9, 17.65) * mm});
            skLineSegment(sketch, "E286", {"start": v(41.05, 46.65) * mm, "end": v(39.07, 44.58) * mm});
            skLineSegment(sketch, "E287", {"start": v(39.07, 44.58) * mm, "end": v(36.99, 41.87) * mm});
            skLineSegment(sketch, "E288", {"start": v(36.99, 41.87) * mm, "end": v(35.06, 39.24) * mm});
            skLineSegment(sketch, "E289", {"start": v(35.06, 39.24) * mm, "end": v(33.55, 37.39) * mm});
            skLineSegment(sketch, "E290", {"start": v(33.55, 37.39) * mm, "end": v(32.52, 36.67) * mm});
            skLineSegment(sketch, "E291", {"start": v(32.52, 36.67) * mm, "end": v(31.39, 36.27) * mm});
            skLineSegment(sketch, "E292", {"start": v(31.39, 36.27) * mm, "end": v(30.37, 36.03) * mm});
            skLineSegment(sketch, "E293", {"start": v(30.37, 36.03) * mm, "end": v(29.69, 35.81) * mm});
            skLineSegment(sketch, "E294", {"start": v(29.69, 35.81) * mm, "end": v(28.14, 34.29) * mm});
            skLineSegment(sketch, "E295", {"start": v(28.14, 34.29) * mm, "end": v(34.22, 28.22) * mm});
            skLineSegment(sketch, "E296", {"start": v(34.22, 28.22) * mm, "end": v(35.74, 29.77) * mm});
            skLineSegment(sketch, "E297", {"start": v(35.74, 29.77) * mm, "end": v(35.96, 30.45) * mm});
            skLineSegment(sketch, "E298", {"start": v(35.96, 30.45) * mm, "end": v(36.2, 31.46) * mm});
            skLineSegment(sketch, "E299", {"start": v(36.2, 31.46) * mm, "end": v(36.6, 32.6) * mm});
            skLineSegment(sketch, "E300", {"start": v(36.6, 32.6) * mm, "end": v(37.32, 33.62) * mm});
            skLineSegment(sketch, "E301", {"start": v(37.32, 33.62) * mm, "end": v(39.16, 35.14) * mm});
            skLineSegment(sketch, "E302", {"start": v(39.16, 35.14) * mm, "end": v(41.78, 37.08) * mm});
            skLineSegment(sketch, "E303", {"start": v(41.78, 37.08) * mm, "end": v(44.48, 39.17) * mm});
            skLineSegment(sketch, "E304", {"start": v(44.48, 39.17) * mm, "end": v(46.6, 41.11) * mm});
            skLineSegment(sketch, "E305", {"start": v(46.6, 41.11) * mm, "end": v(47.4, 42.44) * mm});
            skLineSegment(sketch, "E306", {"start": v(47.4, 42.44) * mm, "end": v(47.58, 43.82) * mm});
            skLineSegment(sketch, "E307", {"start": v(47.58, 43.82) * mm, "end": v(47.2, 45.16) * mm});
            skLineSegment(sketch, "E308", {"start": v(47.2, 45.16) * mm, "end": v(46.32, 46.37) * mm});
            skLineSegment(sketch, "E309", {"start": v(46.32, 46.37) * mm, "end": v(45.06, 47.27) * mm});
            skLineSegment(sketch, "E310", {"start": v(45.06, 47.27) * mm, "end": v(43.7, 47.6) * mm});
            skLineSegment(sketch, "E311", {"start": v(43.7, 47.6) * mm, "end": v(42.34, 47.4) * mm});
            skLineSegment(sketch, "E312", {"start": v(42.34, 47.4) * mm, "end": v(41.05, 46.65) * mm});
            skLineSegment(sketch, "E313", {"start": v(29.54, 35.75) * mm, "end": v(32.88, 32.94) * mm});
            skLineSegment(sketch, "E314", {"start": v(32.88, 32.94) * mm, "end": v(35.7, 29.6) * mm});
            skLineSegment(sketch, "E315", {"start": v(3.54, -0.01) * mm, "end": v(3.25, -1.42) * mm});
            skLineSegment(sketch, "E316", {"start": v(3.25, -1.42) * mm, "end": v(2.47, -2.58) * mm});
            skLineSegment(sketch, "E317", {"start": v(2.47, -2.58) * mm, "end": v(1.32, -3.36) * mm});
            skLineSegment(sketch, "E318", {"start": v(1.32, -3.36) * mm, "end": v(-0.1, -3.64) * mm});
            skLineSegment(sketch, "E319", {"start": v(-0.1, -3.64) * mm, "end": v(-1.52, -3.36) * mm});
            skLineSegment(sketch, "E320", {"start": v(-1.52, -3.36) * mm, "end": v(-2.67, -2.58) * mm});
            skLineSegment(sketch, "E321", {"start": v(-2.67, -2.58) * mm, "end": v(-3.45, -1.42) * mm});
            skLineSegment(sketch, "E322", {"start": v(-3.45, -1.42) * mm, "end": v(-3.74, -0.01) * mm});
            skLineSegment(sketch, "E323", {"start": v(-3.74, -0.01) * mm, "end": v(-3.45, 1.4) * mm});
            skLineSegment(sketch, "E324", {"start": v(-3.45, 1.4) * mm, "end": v(-2.67, 2.56) * mm});
            skLineSegment(sketch, "E325", {"start": v(-2.67, 2.56) * mm, "end": v(-1.52, 3.33) * mm});
            skLineSegment(sketch, "E326", {"start": v(-1.52, 3.33) * mm, "end": v(-0.1, 3.62) * mm});
            skLineSegment(sketch, "E327", {"start": v(-0.1, 3.62) * mm, "end": v(1.32, 3.33) * mm});
            skLineSegment(sketch, "E328", {"start": v(1.32, 3.33) * mm, "end": v(2.47, 2.56) * mm});
            skLineSegment(sketch, "E329", {"start": v(2.47, 2.56) * mm, "end": v(3.25, 1.4) * mm});
            skLineSegment(sketch, "E330", {"start": v(3.25, 1.4) * mm, "end": v(3.54, -0.01) * mm});
            skLineSegment(sketch, "E331", {"start": v(9.65, -2.99) * mm, "end": v(26.1, -2.56) * mm});
            skLineSegment(sketch, "E332", {"start": v(26.1, -2.56) * mm, "end": v(26.82, -2.77) * mm});
            skLineSegment(sketch, "E333", {"start": v(26.82, -2.77) * mm, "end": v(27.64, -3.22) * mm});
            skLineSegment(sketch, "E334", {"start": v(27.64, -3.22) * mm, "end": v(28.5, -3.78) * mm});
            skLineSegment(sketch, "E335", {"start": v(28.5, -3.78) * mm, "end": v(29.36, -4.29) * mm});
            skLineSegment(sketch, "E336", {"start": v(29.36, -4.29) * mm, "end": v(30.78, -4.29) * mm});
            skLineSegment(sketch, "E337", {"start": v(30.78, -4.29) * mm, "end": v(31.08, 0.04) * mm});
            skLineSegment(sketch, "E338", {"start": v(31.08, 0.04) * mm, "end": v(30.78, 4.37) * mm});
            skLineSegment(sketch, "E339", {"start": v(30.78, 4.37) * mm, "end": v(29.29, 4.37) * mm});
            skLineSegment(sketch, "E340", {"start": v(29.29, 4.37) * mm, "end": v(28.5, 3.85) * mm});
            skLineSegment(sketch, "E341", {"start": v(28.5, 3.85) * mm, "end": v(27.69, 3.29) * mm});
            skLineSegment(sketch, "E342", {"start": v(27.69, 3.29) * mm, "end": v(26.91, 2.84) * mm});
            skLineSegment(sketch, "E343", {"start": v(26.91, 2.84) * mm, "end": v(26.22, 2.67) * mm});
            skLineSegment(sketch, "E344", {"start": v(26.22, 2.67) * mm, "end": v(9.66, 2.93) * mm});
            skLineSegment(sketch, "E345", {"start": v(29.33, -4.38) * mm, "end": v(29.55, 0) * mm});
            skLineSegment(sketch, "E346", {"start": v(29.55, 0) * mm, "end": v(29.33, 4.44) * mm});
            skLineSegment(sketch, "E347", {"start": v(62.02, -3.96) * mm, "end": v(59.16, -3.9) * mm});
            skLineSegment(sketch, "E348", {"start": v(59.16, -3.9) * mm, "end": v(55.76, -3.45) * mm});
            skLineSegment(sketch, "E349", {"start": v(55.76, -3.45) * mm, "end": v(52.53, -2.95) * mm});
            skLineSegment(sketch, "E350", {"start": v(52.53, -2.95) * mm, "end": v(50.15, -2.7) * mm});
            skLineSegment(sketch, "E351", {"start": v(50.15, -2.7) * mm, "end": v(48.91, -2.92) * mm});
            skLineSegment(sketch, "E352", {"start": v(48.91, -2.92) * mm, "end": v(47.83, -3.44) * mm});
            skLineSegment(sketch, "E353", {"start": v(47.83, -3.44) * mm, "end": v(46.94, -3.98) * mm});
            skLineSegment(sketch, "E354", {"start": v(46.94, -3.98) * mm, "end": v(46.3, -4.31) * mm});
            skLineSegment(sketch, "E355", {"start": v(46.3, -4.31) * mm, "end": v(44.13, -4.33) * mm});
            skLineSegment(sketch, "E356", {"start": v(44.13, -4.33) * mm, "end": v(44.13, 4.25) * mm});
            skLineSegment(sketch, "E357", {"start": v(44.13, 4.25) * mm, "end": v(46.3, 4.23) * mm});
            skLineSegment(sketch, "E358", {"start": v(46.3, 4.23) * mm, "end": v(46.94, 3.9) * mm});
            skLineSegment(sketch, "E359", {"start": v(46.94, 3.9) * mm, "end": v(47.83, 3.36) * mm});
            skLineSegment(sketch, "E360", {"start": v(47.83, 3.36) * mm, "end": v(48.91, 2.85) * mm});
            skLineSegment(sketch, "E361", {"start": v(48.91, 2.85) * mm, "end": v(50.15, 2.62) * mm});
            skLineSegment(sketch, "E362", {"start": v(50.15, 2.62) * mm, "end": v(52.52, 2.85) * mm});
            skLineSegment(sketch, "E363", {"start": v(52.52, 2.85) * mm, "end": v(55.75, 3.32) * mm});
            skLineSegment(sketch, "E364", {"start": v(55.75, 3.32) * mm, "end": v(59.14, 3.75) * mm});
            skLineSegment(sketch, "E365", {"start": v(59.14, 3.75) * mm, "end": v(62.02, 3.87) * mm});
            skLineSegment(sketch, "E366", {"start": v(62.02, 3.87) * mm, "end": v(63.52, 3.5) * mm});
            skLineSegment(sketch, "E367", {"start": v(63.52, 3.5) * mm, "end": v(64.63, 2.66) * mm});
            skLineSegment(sketch, "E368", {"start": v(64.63, 2.66) * mm, "end": v(65.31, 1.44) * mm});
            skLineSegment(sketch, "E369", {"start": v(65.31, 1.44) * mm, "end": v(65.55, -0.04) * mm});
            skLineSegment(sketch, "E370", {"start": v(65.55, -0.04) * mm, "end": v(65.3, -1.56) * mm});
            skLineSegment(sketch, "E371", {"start": v(65.3, -1.56) * mm, "end": v(64.57, -2.76) * mm});
            skLineSegment(sketch, "E372", {"start": v(64.57, -2.76) * mm, "end": v(63.45, -3.57) * mm});
            skLineSegment(sketch, "E373", {"start": v(63.45, -3.57) * mm, "end": v(62.02, -3.96) * mm});
            skLineSegment(sketch, "E374", {"start": v(46.16, -4.38) * mm, "end": v(46.53, -0.02) * mm});
            skLineSegment(sketch, "E375", {"start": v(46.53, -0.02) * mm, "end": v(46.16, 4.33) * mm});
            skLineSegment(sketch, "E376", {"start": v(-0.1, 44.25) * mm, "end": v(-4.63, 44.03) * mm});
            skLineSegment(sketch, "E377", {"start": v(-4.63, 44.03) * mm, "end": v(-9.04, 43.35) * mm});
            skLineSegment(sketch, "E378", {"start": v(-9.04, 43.35) * mm, "end": v(-13.29, 42.26) * mm});
            skLineSegment(sketch, "E379", {"start": v(-13.29, 42.26) * mm, "end": v(-17.36, 40.77) * mm});
            skLineSegment(sketch, "E380", {"start": v(-17.36, 40.77) * mm, "end": v(-21.24, 38.91) * mm});
            skLineSegment(sketch, "E381", {"start": v(-21.24, 38.91) * mm, "end": v(-24.9, 36.7) * mm});
            skLineSegment(sketch, "E382", {"start": v(-24.9, 36.7) * mm, "end": v(-28.31, 34.15) * mm});
            skLineSegment(sketch, "E383", {"start": v(-28.31, 34.15) * mm, "end": v(-31.46, 31.29) * mm});
            skLineSegment(sketch, "E384", {"start": v(-31.46, 31.29) * mm, "end": v(-34.33, 28.15) * mm});
            skLineSegment(sketch, "E385", {"start": v(-34.33, 28.15) * mm, "end": v(-36.88, 24.74) * mm});
            skLineSegment(sketch, "E386", {"start": v(-36.88, 24.74) * mm, "end": v(-39.1, 21.09) * mm});
            skLineSegment(sketch, "E387", {"start": v(-39.1, 21.09) * mm, "end": v(-40.97, 17.22) * mm});
            skLineSegment(sketch, "E388", {"start": v(-40.97, 17.22) * mm, "end": v(-42.46, 13.15) * mm});
            skLineSegment(sketch, "E389", {"start": v(-42.46, 13.15) * mm, "end": v(-43.55, 8.9) * mm});
            skLineSegment(sketch, "E390", {"start": v(-43.55, 8.9) * mm, "end": v(-44.22, 4.51) * mm});
            skLineSegment(sketch, "E391", {"start": v(-44.22, 4.51) * mm, "end": v(-44.45, -0.01) * mm});
            skLineSegment(sketch, "E392", {"start": v(-44.45, -0.01) * mm, "end": v(-44.22, -4.54) * mm});
            skLineSegment(sketch, "E393", {"start": v(-44.22, -4.54) * mm, "end": v(-43.55, -8.93) * mm});
            skLineSegment(sketch, "E394", {"start": v(-43.55, -8.93) * mm, "end": v(-42.46, -13.17) * mm});
            skLineSegment(sketch, "E395", {"start": v(-42.46, -13.17) * mm, "end": v(-40.97, -17.24) * mm});
            skLineSegment(sketch, "E396", {"start": v(-40.97, -17.24) * mm, "end": v(-39.1, -21.11) * mm});
            skLineSegment(sketch, "E397", {"start": v(-39.1, -21.11) * mm, "end": v(-36.88, -24.76) * mm});
            skLineSegment(sketch, "E398", {"start": v(-36.88, -24.76) * mm, "end": v(-34.33, -28.17) * mm});
            skLineSegment(sketch, "E399", {"start": v(-34.33, -28.17) * mm, "end": v(-31.46, -31.31) * mm});
            skLineSegment(sketch, "E400", {"start": v(-31.46, -31.31) * mm, "end": v(-28.31, -34.17) * mm});
            skLineSegment(sketch, "E401", {"start": v(-28.31, -34.17) * mm, "end": v(-24.9, -36.72) * mm});
            skLineSegment(sketch, "E402", {"start": v(-24.9, -36.72) * mm, "end": v(-21.24, -38.93) * mm});
            skLineSegment(sketch, "E403", {"start": v(-21.24, -38.93) * mm, "end": v(-17.36, -40.8) * mm});
            skLineSegment(sketch, "E404", {"start": v(-17.36, -40.8) * mm, "end": v(-13.29, -42.29) * mm});
            skLineSegment(sketch, "E405", {"start": v(-13.29, -42.29) * mm, "end": v(-9.04, -43.38) * mm});
            skLineSegment(sketch, "E406", {"start": v(-9.04, -43.38) * mm, "end": v(-4.63, -44.05) * mm});
            skLineSegment(sketch, "E407", {"start": v(-4.63, -44.05) * mm, "end": v(-0.1, -44.28) * mm});
            skLineSegment(sketch, "E408", {"start": v(-0.1, -44.28) * mm, "end": v(4.43, -44.05) * mm});
            skLineSegment(sketch, "E409", {"start": v(4.43, -44.05) * mm, "end": v(8.84, -43.38) * mm});
            skLineSegment(sketch, "E410", {"start": v(8.84, -43.38) * mm, "end": v(13.09, -42.29) * mm});
            skLineSegment(sketch, "E411", {"start": v(13.09, -42.29) * mm, "end": v(17.16, -40.8) * mm});
            skLineSegment(sketch, "E412", {"start": v(17.16, -40.8) * mm, "end": v(21.04, -38.93) * mm});
            skLineSegment(sketch, "E413", {"start": v(21.04, -38.93) * mm, "end": v(24.7, -36.72) * mm});
            skLineSegment(sketch, "E414", {"start": v(24.7, -36.72) * mm, "end": v(28.11, -34.17) * mm});
            skLineSegment(sketch, "E415", {"start": v(28.11, -34.17) * mm, "end": v(31.26, -31.31) * mm});
            skLineSegment(sketch, "E416", {"start": v(31.26, -31.31) * mm, "end": v(34.13, -28.17) * mm});
            skLineSegment(sketch, "E417", {"start": v(34.13, -28.17) * mm, "end": v(36.68, -24.76) * mm});
            skLineSegment(sketch, "E418", {"start": v(36.68, -24.76) * mm, "end": v(38.9, -21.11) * mm});
            skLineSegment(sketch, "E419", {"start": v(38.9, -21.11) * mm, "end": v(40.77, -17.24) * mm});
            skLineSegment(sketch, "E420", {"start": v(40.77, -17.24) * mm, "end": v(42.26, -13.17) * mm});
            skLineSegment(sketch, "E421", {"start": v(42.26, -13.17) * mm, "end": v(43.35, -8.93) * mm});
            skLineSegment(sketch, "E422", {"start": v(43.35, -8.93) * mm, "end": v(44.02, -4.54) * mm});
            skLineSegment(sketch, "E423", {"start": v(44.02, -4.54) * mm, "end": v(44.25, -0.01) * mm});
            skLineSegment(sketch, "E424", {"start": v(44.25, -0.01) * mm, "end": v(44.02, 4.51) * mm});
            skLineSegment(sketch, "E425", {"start": v(44.02, 4.51) * mm, "end": v(43.35, 8.9) * mm});
            skLineSegment(sketch, "E426", {"start": v(43.35, 8.9) * mm, "end": v(42.26, 13.15) * mm});
            skLineSegment(sketch, "E427", {"start": v(42.26, 13.15) * mm, "end": v(40.77, 17.22) * mm});
            skLineSegment(sketch, "E428", {"start": v(40.77, 17.22) * mm, "end": v(38.9, 21.09) * mm});
            skLineSegment(sketch, "E429", {"start": v(38.9, 21.09) * mm, "end": v(36.68, 24.74) * mm});
            skLineSegment(sketch, "E430", {"start": v(36.68, 24.74) * mm, "end": v(34.13, 28.15) * mm});
            skLineSegment(sketch, "E431", {"start": v(34.13, 28.15) * mm, "end": v(31.26, 31.29) * mm});
            skLineSegment(sketch, "E432", {"start": v(31.26, 31.29) * mm, "end": v(28.11, 34.15) * mm});
            skLineSegment(sketch, "E433", {"start": v(28.11, 34.15) * mm, "end": v(24.7, 36.7) * mm});
            skLineSegment(sketch, "E434", {"start": v(24.7, 36.7) * mm, "end": v(21.04, 38.91) * mm});
            skLineSegment(sketch, "E435", {"start": v(21.04, 38.91) * mm, "end": v(17.16, 40.77) * mm});
            skLineSegment(sketch, "E436", {"start": v(17.16, 40.77) * mm, "end": v(13.09, 42.26) * mm});
            skLineSegment(sketch, "E437", {"start": v(13.09, 42.26) * mm, "end": v(8.84, 43.35) * mm});
            skLineSegment(sketch, "E438", {"start": v(8.84, 43.35) * mm, "end": v(4.43, 44.03) * mm});
            skLineSegment(sketch, "E439", {"start": v(4.43, 44.03) * mm, "end": v(-0.1, 44.25) * mm});
            skLineSegment(sketch, "E440", {"start": v(-0.1, 31.24) * mm, "end": v(6.21, 30.6) * mm});
            skLineSegment(sketch, "E441", {"start": v(6.21, 30.6) * mm, "end": v(12.09, 28.78) * mm});
            skLineSegment(sketch, "E442", {"start": v(12.09, 28.78) * mm, "end": v(17.4, 25.9) * mm});
            skLineSegment(sketch, "E443", {"start": v(17.4, 25.9) * mm, "end": v(22.04, 22.08) * mm});
            skLineSegment(sketch, "E444", {"start": v(22.04, 22.08) * mm, "end": v(25.86, 17.46) * mm});
            skLineSegment(sketch, "E445", {"start": v(25.86, 17.46) * mm, "end": v(28.75, 12.15) * mm});
            skLineSegment(sketch, "E446", {"start": v(28.75, 12.15) * mm, "end": v(30.58, 6.29) * mm});
            skLineSegment(sketch, "E447", {"start": v(30.58, 6.29) * mm, "end": v(31.21, -0.01) * mm});
            skLineSegment(sketch, "E448", {"start": v(31.21, -0.01) * mm, "end": v(30.58, -6.3) * mm});
            skLineSegment(sketch, "E449", {"start": v(30.58, -6.3) * mm, "end": v(28.75, -12.17) * mm});
            skLineSegment(sketch, "E450", {"start": v(28.75, -12.17) * mm, "end": v(25.86, -17.48) * mm});
            skLineSegment(sketch, "E451", {"start": v(25.86, -17.48) * mm, "end": v(22.04, -22.1) * mm});
            skLineSegment(sketch, "E452", {"start": v(22.04, -22.1) * mm, "end": v(17.4, -25.92) * mm});
            skLineSegment(sketch, "E453", {"start": v(17.4, -25.92) * mm, "end": v(12.09, -28.8) * mm});
            skLineSegment(sketch, "E454", {"start": v(12.09, -28.8) * mm, "end": v(6.21, -30.63) * mm});
            skLineSegment(sketch, "E455", {"start": v(6.21, -30.63) * mm, "end": v(-0.1, -31.26) * mm});
            skLineSegment(sketch, "E456", {"start": v(-0.1, -31.26) * mm, "end": v(-6.4, -30.63) * mm});
            skLineSegment(sketch, "E457", {"start": v(-6.4, -30.63) * mm, "end": v(-12.29, -28.8) * mm});
            skLineSegment(sketch, "E458", {"start": v(-12.29, -28.8) * mm, "end": v(-17.6, -25.92) * mm});
            skLineSegment(sketch, "E459", {"start": v(-17.6, -25.92) * mm, "end": v(-22.24, -22.1) * mm});
            skLineSegment(sketch, "E460", {"start": v(-22.24, -22.1) * mm, "end": v(-26.06, -17.48) * mm});
            skLineSegment(sketch, "E461", {"start": v(-26.06, -17.48) * mm, "end": v(-28.95, -12.17) * mm});
            skLineSegment(sketch, "E462", {"start": v(-28.95, -12.17) * mm, "end": v(-30.78, -6.3) * mm});
            skLineSegment(sketch, "E463", {"start": v(-30.78, -6.3) * mm, "end": v(-31.41, -0.01) * mm});
            skLineSegment(sketch, "E464", {"start": v(-31.41, -0.01) * mm, "end": v(-30.78, 6.29) * mm});
            skLineSegment(sketch, "E465", {"start": v(-30.78, 6.29) * mm, "end": v(-28.95, 12.15) * mm});
            skLineSegment(sketch, "E466", {"start": v(-28.95, 12.15) * mm, "end": v(-26.06, 17.46) * mm});
            skLineSegment(sketch, "E467", {"start": v(-26.06, 17.46) * mm, "end": v(-22.24, 22.08) * mm});
            skLineSegment(sketch, "E468", {"start": v(-22.24, 22.08) * mm, "end": v(-17.6, 25.9) * mm});
            skLineSegment(sketch, "E469", {"start": v(-17.6, 25.9) * mm, "end": v(-12.29, 28.78) * mm});
            skLineSegment(sketch, "E470", {"start": v(-12.29, 28.78) * mm, "end": v(-6.4, 30.6) * mm});
            skLineSegment(sketch, "E471", {"start": v(-6.4, 30.6) * mm, "end": v(-0.1, 31.24) * mm});
            skLineSegment(sketch, "E472", {"start": v(-2.76, -2.56) * mm, "end": v(-5.7, -5.5) * mm});
            skLineSegment(sketch, "E473", {"start": v(6.03, 6.2) * mm, "end": v(2.4, 2.58) * mm});
            skLineSegment(sketch, "E474", {"start": v(2.65, -2.35) * mm, "end": v(5.6, -5.28) * mm});
            skLineSegment(sketch, "E475", {"start": v(-6.14, 6.43) * mm, "end": v(-2.5, 2.8) * mm});
            skLineSegment(sketch, "E476", {"start": v(-3.75, -0.01) * mm, "end": v(-8.24, -0.01) * mm});
            skLineSegment(sketch, "E477", {"start": v(8.35, -0.01) * mm, "end": v(3.56, -0.01) * mm});
            skLineSegment(sketch, "E478", {"start": v(-0.1, -3.68) * mm, "end": v(-0.1, -7.83) * mm});
            skLineSegment(sketch, "E479", {"start": v(-0.1, 8.73) * mm, "end": v(-0.1, 3.6) * mm});
            skLineSegment(sketch, "E480", {"start": v(32.3, -0.01) * mm, "end": v(31.64, -6.53) * mm});
            skLineSegment(sketch, "E481", {"start": v(31.64, -6.53) * mm, "end": v(29.75, -12.6) * mm});
            skLineSegment(sketch, "E482", {"start": v(29.75, -12.6) * mm, "end": v(26.76, -18.09) * mm});
            skLineSegment(sketch, "E483", {"start": v(26.76, -18.09) * mm, "end": v(22.8, -22.87) * mm});
            skLineSegment(sketch, "E484", {"start": v(22.8, -22.87) * mm, "end": v(18.01, -26.82) * mm});
            skLineSegment(sketch, "E485", {"start": v(18.01, -26.82) * mm, "end": v(12.5, -29.8) * mm});
            skLineSegment(sketch, "E486", {"start": v(12.5, -29.8) * mm, "end": v(6.43, -31.69) * mm});
            skLineSegment(sketch, "E487", {"start": v(6.43, -31.69) * mm, "end": v(-0.1, -32.34) * mm});
            skLineSegment(sketch, "E488", {"start": v(-0.1, -32.34) * mm, "end": v(-6.63, -31.69) * mm});
            skLineSegment(sketch, "E489", {"start": v(-6.63, -31.69) * mm, "end": v(-12.7, -29.8) * mm});
            skLineSegment(sketch, "E490", {"start": v(-12.7, -29.8) * mm, "end": v(-18.21, -26.82) * mm});
            skLineSegment(sketch, "E491", {"start": v(-18.21, -26.82) * mm, "end": v(-23, -22.87) * mm});
            skLineSegment(sketch, "E492", {"start": v(-23, -22.87) * mm, "end": v(-26.96, -18.09) * mm});
            skLineSegment(sketch, "E493", {"start": v(-26.96, -18.09) * mm, "end": v(-29.95, -12.6) * mm});
            skLineSegment(sketch, "E494", {"start": v(-29.95, -12.6) * mm, "end": v(-31.84, -6.53) * mm});
            skLineSegment(sketch, "E495", {"start": v(-31.84, -6.53) * mm, "end": v(-32.5, -0.01) * mm});
            skLineSegment(sketch, "E496", {"start": v(-32.5, -0.01) * mm, "end": v(-31.84, 6.5) * mm});
            skLineSegment(sketch, "E497", {"start": v(-31.84, 6.5) * mm, "end": v(-29.95, 12.57) * mm});
            skLineSegment(sketch, "E498", {"start": v(-29.95, 12.57) * mm, "end": v(-26.96, 18.06) * mm});
            skLineSegment(sketch, "E499", {"start": v(-26.96, 18.06) * mm, "end": v(-23, 22.85) * mm});
            skLineSegment(sketch, "E500", {"start": v(-23, 22.85) * mm, "end": v(-18.21, 26.8) * mm});
            skLineSegment(sketch, "E501", {"start": v(-18.21, 26.8) * mm, "end": v(-12.7, 29.78) * mm});
            skLineSegment(sketch, "E502", {"start": v(-12.7, 29.78) * mm, "end": v(-6.63, 31.66) * mm});
            skLineSegment(sketch, "E503", {"start": v(-6.63, 31.66) * mm, "end": v(-0.1, 32.32) * mm});
            skLineSegment(sketch, "E504", {"start": v(-0.1, 32.32) * mm, "end": v(6.43, 31.66) * mm});
            skLineSegment(sketch, "E505", {"start": v(6.43, 31.66) * mm, "end": v(12.5, 29.78) * mm});
            skLineSegment(sketch, "E506", {"start": v(12.5, 29.78) * mm, "end": v(18.01, 26.8) * mm});
            skLineSegment(sketch, "E507", {"start": v(18.01, 26.8) * mm, "end": v(22.8, 22.85) * mm});
            skLineSegment(sketch, "E508", {"start": v(22.8, 22.85) * mm, "end": v(26.76, 18.06) * mm});
            skLineSegment(sketch, "E509", {"start": v(26.76, 18.06) * mm, "end": v(29.75, 12.57) * mm});
            skLineSegment(sketch, "E510", {"start": v(29.75, 12.57) * mm, "end": v(31.64, 6.5) * mm});
            skLineSegment(sketch, "E511", {"start": v(31.64, 6.5) * mm, "end": v(32.3, -0.01) * mm});
            skLineSegment(sketch, "E512", {"start": v(-0.1, 10.82) * mm, "end": v(-2.29, 10.6) * mm});
            skLineSegment(sketch, "E513", {"start": v(-2.29, 10.6) * mm, "end": v(-4.33, 9.97) * mm});
            skLineSegment(sketch, "E514", {"start": v(-4.33, 9.97) * mm, "end": v(-6.17, 8.97) * mm});
            skLineSegment(sketch, "E515", {"start": v(-6.17, 8.97) * mm, "end": v(-7.78, 7.65) * mm});
            skLineSegment(sketch, "E516", {"start": v(-7.78, 7.65) * mm, "end": v(-9.1, 6.05) * mm});
            skLineSegment(sketch, "E517", {"start": v(-9.1, 6.05) * mm, "end": v(-10.1, 4.2) * mm});
            skLineSegment(sketch, "E518", {"start": v(-10.1, 4.2) * mm, "end": v(-10.73, 2.17) * mm});
            skLineSegment(sketch, "E519", {"start": v(-10.73, 2.17) * mm, "end": v(-10.96, -0.01) * mm});
            skLineSegment(sketch, "E520", {"start": v(-10.96, -0.01) * mm, "end": v(-10.73, -2.2) * mm});
            skLineSegment(sketch, "E521", {"start": v(-10.73, -2.2) * mm, "end": v(-10.1, -4.23) * mm});
            skLineSegment(sketch, "E522", {"start": v(-10.1, -4.23) * mm, "end": v(-9.1, -6.07) * mm});
            skLineSegment(sketch, "E523", {"start": v(-9.1, -6.07) * mm, "end": v(-7.78, -7.67) * mm});
            skLineSegment(sketch, "E524", {"start": v(-7.78, -7.67) * mm, "end": v(-6.17, -9) * mm});
            skLineSegment(sketch, "E525", {"start": v(-6.17, -9) * mm, "end": v(-4.33, -10) * mm});
            skLineSegment(sketch, "E526", {"start": v(-4.33, -10) * mm, "end": v(-2.29, -10.63) * mm});
            skLineSegment(sketch, "E527", {"start": v(-2.29, -10.63) * mm, "end": v(-0.1, -10.85) * mm});
            skLineSegment(sketch, "E528", {"start": v(-0.1, -10.85) * mm, "end": v(2.09, -10.63) * mm});
            skLineSegment(sketch, "E529", {"start": v(2.09, -10.63) * mm, "end": v(4.13, -10) * mm});
            skLineSegment(sketch, "E530", {"start": v(4.13, -10) * mm, "end": v(5.97, -9) * mm});
            skLineSegment(sketch, "E531", {"start": v(5.97, -9) * mm, "end": v(7.58, -7.67) * mm});
            skLineSegment(sketch, "E532", {"start": v(7.58, -7.67) * mm, "end": v(8.9, -6.07) * mm});
            skLineSegment(sketch, "E533", {"start": v(8.9, -6.07) * mm, "end": v(9.9, -4.23) * mm});
            skLineSegment(sketch, "E534", {"start": v(9.9, -4.23) * mm, "end": v(10.54, -2.2) * mm});
            skLineSegment(sketch, "E535", {"start": v(10.54, -2.2) * mm, "end": v(10.76, -0.01) * mm});
            skLineSegment(sketch, "E536", {"start": v(10.76, -0.01) * mm, "end": v(10.54, 2.17) * mm});
            skLineSegment(sketch, "E537", {"start": v(10.54, 2.17) * mm, "end": v(9.9, 4.2) * mm});
            skLineSegment(sketch, "E538", {"start": v(9.9, 4.2) * mm, "end": v(8.9, 6.05) * mm});
            skLineSegment(sketch, "E539", {"start": v(8.9, 6.05) * mm, "end": v(7.58, 7.65) * mm});
            skLineSegment(sketch, "E540", {"start": v(7.58, 7.65) * mm, "end": v(5.97, 8.97) * mm});
            skLineSegment(sketch, "E541", {"start": v(5.97, 8.97) * mm, "end": v(4.13, 9.97) * mm});
            skLineSegment(sketch, "E542", {"start": v(4.13, 9.97) * mm, "end": v(2.09, 10.6) * mm});
            skLineSegment(sketch, "E543", {"start": v(2.09, 10.6) * mm, "end": v(-0.1, 10.82) * mm});
            skLineSegment(sketch, "E544", {"start": v(-0.1, 7.29) * mm, "end": v(2.75, 6.72) * mm});
            skLineSegment(sketch, "E545", {"start": v(2.75, 6.72) * mm, "end": v(5.07, 5.15) * mm});
            skLineSegment(sketch, "E546", {"start": v(5.07, 5.15) * mm, "end": v(6.64, 2.83) * mm});
            skLineSegment(sketch, "E547", {"start": v(6.64, 2.83) * mm, "end": v(7.22, -0.01) * mm});
            skLineSegment(sketch, "E548", {"start": v(7.22, -0.01) * mm, "end": v(6.64, -2.85) * mm});
            skLineSegment(sketch, "E549", {"start": v(6.64, -2.85) * mm, "end": v(5.07, -5.17) * mm});
            skLineSegment(sketch, "E550", {"start": v(5.07, -5.17) * mm, "end": v(2.75, -6.74) * mm});
            skLineSegment(sketch, "E551", {"start": v(2.75, -6.74) * mm, "end": v(-0.1, -7.31) * mm});
            skLineSegment(sketch, "E552", {"start": v(-0.1, -7.31) * mm, "end": v(-2.95, -6.74) * mm});
            skLineSegment(sketch, "E553", {"start": v(-2.95, -6.74) * mm, "end": v(-5.27, -5.17) * mm});
            skLineSegment(sketch, "E554", {"start": v(-5.27, -5.17) * mm, "end": v(-6.84, -2.85) * mm});
            skLineSegment(sketch, "E555", {"start": v(-6.84, -2.85) * mm, "end": v(-7.41, -0.01) * mm});
            skLineSegment(sketch, "E556", {"start": v(-7.41, -0.01) * mm, "end": v(-6.84, 2.83) * mm});
            skLineSegment(sketch, "E557", {"start": v(-6.84, 2.83) * mm, "end": v(-5.27, 5.15) * mm});
            skLineSegment(sketch, "E558", {"start": v(-5.27, 5.15) * mm, "end": v(-2.95, 6.72) * mm});
            skLineSegment(sketch, "E559", {"start": v(-2.95, 6.72) * mm, "end": v(-0.1, 7.29) * mm});
            skSolve(sketch);
        }
        {
            var Q0;
            Q0=qSketchRegion(id+"F0",true);
            extrude(context, id + "F1", {"entities" : qUnion([Q0]), "depth" : 3.17 * mm});
        }
        {
            var Q0;
            Q0=qSketchRegion(id+"F0",true);
            var Q1;
            {var subQ6=sQuery(id+"F0.wireOp",EDGE,"E1");Q1=makeQuery(id+"F0.imprint","IMPRINT",FACE,{"disambiguationData":[TD([[makeQuery(id+"F0.imprint","IMPRINT",EDGE,{"derivedFrom":subQ6}),-1.0]])]});}
            var Q2;
            {var subQ83=sQuery(id+"F0.wireOp",EDGE,"E441");Q2=makeQuery(id+"F0.imprint","IMPRINT",FACE,{"disambiguationData":[TD([[makeQuery(id+"F0.imprint","IMPRINT",EDGE,{"derivedFrom":subQ83}),1.0]])]});}
            var Q3;
            {var subQ1=sQuery(id+"F0.wireOp",EDGE,"E5");Q3=makeQuery(id+"F0.imprint","IMPRINT",FACE,{"disambiguationData":[TD([[makeQuery(id+"F0.imprint","IMPRINT",EDGE,{"derivedFrom":subQ1}),-1.0]])]});}
            var Q4;
            {var subQ19=sQuery(id+"F0.wireOp",EDGE,"E544");Q4=makeQuery(id+"F0.imprint","IMPRINT",FACE,{"disambiguationData":[TD([[makeQuery(id+"F0.imprint","IMPRINT",EDGE,{"derivedFrom":subQ19}),1.0]])]});}
            var Q5;
            {var subQ12=sQuery(id+"F0.wireOp",EDGE,"E226");Q5=makeQuery(id+"F0.imprint","IMPRINT",FACE,{"disambiguationData":[TD([[makeQuery(id+"F0.imprint","IMPRINT",EDGE,{"derivedFrom":subQ12}),-1.0]])]});}
            var Q6;
            {var subQ4=sQuery(id+"F0.wireOp",EDGE,"E230");Q6=makeQuery(id+"F0.imprint","IMPRINT",FACE,{"disambiguationData":[TD([[makeQuery(id+"F0.imprint","IMPRINT",EDGE,{"derivedFrom":subQ4}),-1.0]])]});}
            var Q7;
            {var subQ10=sQuery(id+"F0.wireOp",EDGE,"E181");Q7=makeQuery(id+"F0.imprint","IMPRINT",FACE,{"disambiguationData":[TD([[makeQuery(id+"F0.imprint","IMPRINT",EDGE,{"derivedFrom":subQ10}),-1.0]])]});}
            var Q8;
            {var subQ10=sQuery(id+"F0.wireOp",EDGE,"E91");Q8=makeQuery(id+"F0.imprint","IMPRINT",FACE,{"disambiguationData":[TD([[makeQuery(id+"F0.imprint","IMPRINT",EDGE,{"derivedFrom":subQ10}),-1.0]])]});}
            var Q9;
            {var subQ1=sQuery(id+"F0.wireOp",EDGE,"E271");Q9=makeQuery(id+"F0.imprint","IMPRINT",FACE,{"disambiguationData":[TD([[makeQuery(id+"F0.imprint","IMPRINT",EDGE,{"derivedFrom":subQ1}),-1.0]])]});}
            var Q10;
            {var subQ6=sQuery(id+"F0.wireOp",EDGE,"E332");Q10=makeQuery(id+"F0.imprint","IMPRINT",FACE,{"disambiguationData":[TD([[makeQuery(id+"F0.imprint","IMPRINT",EDGE,{"derivedFrom":subQ6}),1.0]])]});}
            var Q11;
            {var subQ1=sQuery(id+"F0.wireOp",EDGE,"E136");Q11=makeQuery(id+"F0.imprint","IMPRINT",FACE,{"disambiguationData":[TD([[makeQuery(id+"F0.imprint","IMPRINT",EDGE,{"derivedFrom":subQ1}),-1.0]])]});}
            var Q12;
            {var subQ9=sQuery(id+"F0.wireOp",EDGE,"E46");Q12=makeQuery(id+"F0.imprint","IMPRINT",FACE,{"disambiguationData":[TD([[makeQuery(id+"F0.imprint","IMPRINT",EDGE,{"derivedFrom":subQ9}),-1.0]])]});}
            var Q13;
            {var subQ7=sQuery(id+"F0.wireOp",EDGE,"E50");var subQ8=sQuery(id+"F0.wireOp",EDGE,"E49");var subQ9=makeQuery(id+"F0.imprint","INTERSECT",VERTEX,{"derivedFrom":[subQ8,subQ7]});Q13=makeQuery(id+"F0.imprint","IMPRINT",FACE,{"disambiguationData":[TD([[makeQuery(id+"F0.imprint","IMPRINT",EDGE,{"disambiguationData":[TD([[subQ9,1.0]])],"derivedFrom":subQ8}),-1.0]])]});}
            var Q14;
            {var subQ7=sQuery(id+"F0.wireOp",EDGE,"E140");var subQ8=sQuery(id+"F0.wireOp",EDGE,"E139");var subQ9=makeQuery(id+"F0.imprint","INTERSECT",VERTEX,{"derivedFrom":[subQ8,subQ7]});Q14=makeQuery(id+"F0.imprint","IMPRINT",FACE,{"disambiguationData":[TD([[makeQuery(id+"F0.imprint","IMPRINT",EDGE,{"disambiguationData":[TD([[subQ9,1.0]])],"derivedFrom":subQ8}),-1.0]])]});}
            var Q15;
            {var subQ12=sQuery(id+"F0.wireOp",EDGE,"E336");Q15=makeQuery(id+"F0.imprint","IMPRINT",FACE,{"disambiguationData":[TD([[makeQuery(id+"F0.imprint","IMPRINT",EDGE,{"derivedFrom":subQ12}),1.0]])]});}
            var Q16;
            {var subQ6=sQuery(id+"F0.wireOp",EDGE,"E275");var subQ9=sQuery(id+"F0.wireOp",EDGE,"E274");var subQ10=makeQuery(id+"F0.imprint","INTERSECT",VERTEX,{"derivedFrom":[subQ9,subQ6]});Q16=makeQuery(id+"F0.imprint","IMPRINT",FACE,{"disambiguationData":[TD([[makeQuery(id+"F0.imprint","IMPRINT",EDGE,{"disambiguationData":[TD([[subQ10,1.0]])],"derivedFrom":subQ9}),-1.0]])]});}
            var Q17;
            {var subQ9=sQuery(id+"F0.wireOp",EDGE,"E95");var subQ10=sQuery(id+"F0.wireOp",EDGE,"E94");var subQ11=makeQuery(id+"F0.imprint","INTERSECT",VERTEX,{"derivedFrom":[subQ10,subQ9]});Q17=makeQuery(id+"F0.imprint","IMPRINT",FACE,{"disambiguationData":[TD([[makeQuery(id+"F0.imprint","IMPRINT",EDGE,{"disambiguationData":[TD([[subQ11,1.0]])],"derivedFrom":subQ10}),-1.0]])]});}
            var Q18;
            {var subQ7=sQuery(id+"F0.wireOp",EDGE,"E185");var subQ8=sQuery(id+"F0.wireOp",EDGE,"E184");var subQ9=makeQuery(id+"F0.imprint","INTERSECT",VERTEX,{"derivedFrom":[subQ8,subQ7]});Q18=makeQuery(id+"F0.imprint","IMPRINT",FACE,{"disambiguationData":[TD([[makeQuery(id+"F0.imprint","IMPRINT",EDGE,{"disambiguationData":[TD([[subQ9,1.0]])],"derivedFrom":subQ8}),-1.0]])]});}
            extrude(context, id + "F2", {"entities" : qUnion([Q0, Q1, Q2, Q3, Q4, Q5, Q6, Q7, Q8, Q9, Q10, Q11, Q12, Q13, Q14, Q15, Q16, Q17, Q18]), "depth" : 3.17 * mm});
        }
    });
